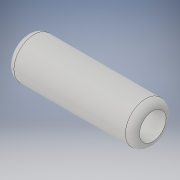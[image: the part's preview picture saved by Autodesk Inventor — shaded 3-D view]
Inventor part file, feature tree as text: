
AUTODESK INVENTOR PART (.ipt)
format: ipt  version: 2017 (Build 210142000, 142)  size: 125,440 bytes
history: native  units: in
note: dims shown in document units (in); Inventor stores cm internally (conversion verified against a paired STEP export)
features: fillet x2, revolve x1, sketch x1
ambient origin geometry x8: Origin, YZ Plane, XZ Plane, XY Plane, X Axis, Y Axis, Z Axis, Center Point
bodies: Body1 (feature_tree)
feature tree (4):
  revolve  "Revolution2"  [1 undecoded]
  fillet  "Fillet1"  Radius=4.313in
  fillet  "Fillet2"  Radius=0.4375in
  sketch  "Sketch3"  dims[d163=4.469in d164=0.25in d165=4.313in d166=0.4375in d167=0.0375in d168=90.0deg d169=0.25in d170=0.25in]
note: 1 required parameter value undecoded (feature->parameter linkage not recoverable at this tier; creation-order binding heuristic only, values carry confidence <= 0.55)
